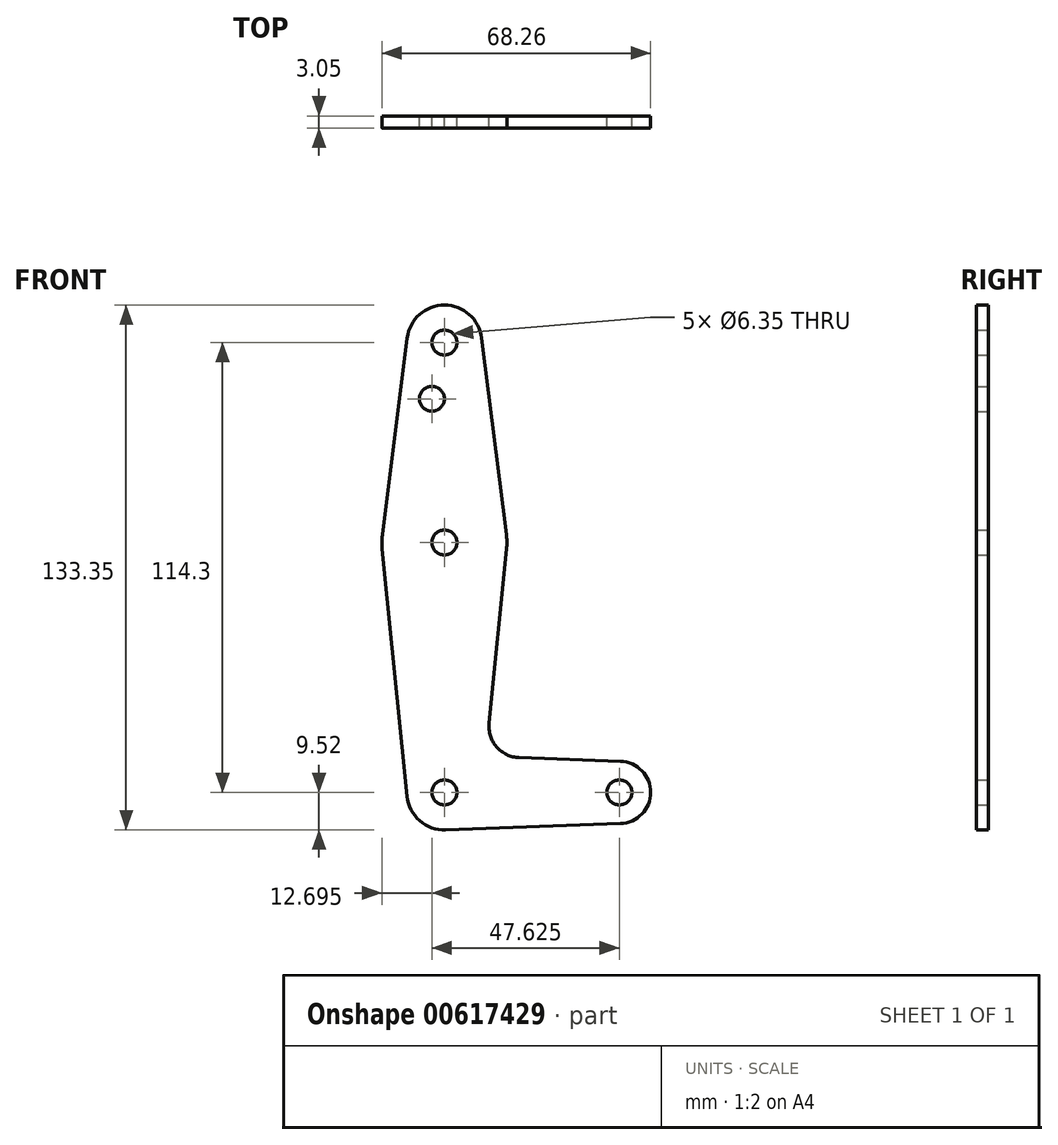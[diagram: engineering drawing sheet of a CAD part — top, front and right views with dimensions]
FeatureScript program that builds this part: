
annotation { "Feature Type Name" : "Feature", "Feature Type Description" : "" }
export const myFeature = defineFeature(function(context is Context, id is Id, definition is map)
    precondition{}
    {
        {
            var Q0;
            Q0=qCreatedBy(makeId("Front.planeOp"),FACE);
            var sketch = newSketch(context, id + "F0", { "sketchPlane" : qUnion([Q0])});
            skLineSegment(sketch, "E0", {"start": v(0, 0) * mm, "end": v(44.45, 0) * mm, "construction": true});
            skLineSegment(sketch, "E1", {"start": v(0, 0) * mm, "end": v(0, 114.3) * mm, "construction": true});
            skCircle(sketch, "E2", {"center": v(0, 114.3) * mm, "radius": 9.53 * mm});
            skCircle(sketch, "E3", {"center": v(0, 63.5) * mm, "radius": 15.88 * mm});
            skCircle(sketch, "E4", {"center": v(0, 0) * mm, "radius": 9.53 * mm});
            skCircle(sketch, "E5", {"center": v(44.45, 0) * mm, "radius": 7.94 * mm});
            skLineSegment(sketch, "E6", {"start": v(-9.45, 115.5) * mm, "end": v(-15.75, 65.48) * mm});
            skLineSegment(sketch, "E7", {"start": v(9.45, 115.5) * mm, "end": v(15.75, 65.48) * mm});
            skLineSegment(sketch, "E8", {"start": v(-15.8, 61.91) * mm, "end": v(-9.48, -0.95) * mm});
            skLineSegment(sketch, "E9", {"start": v(0.34, -9.52) * mm, "end": v(44.73, -7.93) * mm});
            skLineSegment(sketch, "E10", {"start": v(18.97, 8.85) * mm, "end": v(44.73, 7.93) * mm});
            skLineSegment(sketch, "E11", {"start": v(15.8, 61.91) * mm, "end": v(11.34, 17.6) * mm});
            skArc(sketch, "E12.filletArc", {"start": v(11.34, 17.6) * mm, "mid": v(13.26, 11.57) * mm, "end": v(18.97, 8.85) * mm});
            skCircle(sketch, "E13", {"center": v(0, 114.3) * mm, "radius": 3.18 * mm});
            skCircle(sketch, "E14", {"center": v(0, 63.5) * mm, "radius": 3.18 * mm});
            skCircle(sketch, "E15", {"center": v(-3.18, 100.01) * mm, "radius": 3.18 * mm});
            skCircle(sketch, "E16", {"center": v(0, 0) * mm, "radius": 3.18 * mm});
            skCircle(sketch, "E17", {"center": v(44.45, 0) * mm, "radius": 3.18 * mm});
            skSolve(sketch);
        }
        {
            var Q0;
            Q0=makeQuery(id+"F0.imprint","IMPRINT",FACE,{"disambiguationData":[TD([[makeQuery(id+"F0.imprint","IMPRINT",EDGE,{"derivedFrom":sQuery(id+"F0.wireOp",EDGE,"E13")}),-1.0]])]});
            var Q1;
            {var subQ0=sQuery(id+"F0.wireOp",EDGE,"E6");Q1=makeQuery(id+"F0.imprint","IMPRINT",FACE,{"disambiguationData":[TD([[makeQuery(id+"F0.imprint","IMPRINT",EDGE,{"derivedFrom":subQ0}),1.0]])]});}
            var Q2;
            Q2=makeQuery(id+"F0.imprint","IMPRINT",FACE,{"disambiguationData":[TD([[makeQuery(id+"F0.imprint","IMPRINT",EDGE,{"derivedFrom":sQuery(id+"F0.wireOp",EDGE,"E14")}),-1.0]])]});
            var Q3;
            {var subQ3=sQuery(id+"F0.wireOp",EDGE,"E8");Q3=makeQuery(id+"F0.imprint","IMPRINT",FACE,{"disambiguationData":[TD([[makeQuery(id+"F0.imprint","IMPRINT",EDGE,{"derivedFrom":subQ3}),1.0]])]});}
            var Q4;
            Q4=makeQuery(id+"F0.imprint","IMPRINT",FACE,{"disambiguationData":[TD([[makeQuery(id+"F0.imprint","IMPRINT",EDGE,{"derivedFrom":sQuery(id+"F0.wireOp",EDGE,"E16")}),-1.0]])]});
            var Q5;
            Q5=makeQuery(id+"F0.imprint","IMPRINT",FACE,{"disambiguationData":[TD([[makeQuery(id+"F0.imprint","IMPRINT",EDGE,{"derivedFrom":sQuery(id+"F0.wireOp",EDGE,"E17")}),-1.0]])]});
            extrude(context, id + "F1", {"entities" : qUnion([Q0, Q1, Q2, Q3, Q4, Q5]), "depth" : 3.05 * mm, "offsetDistance" : 25.4 * mm});
        }
    });
